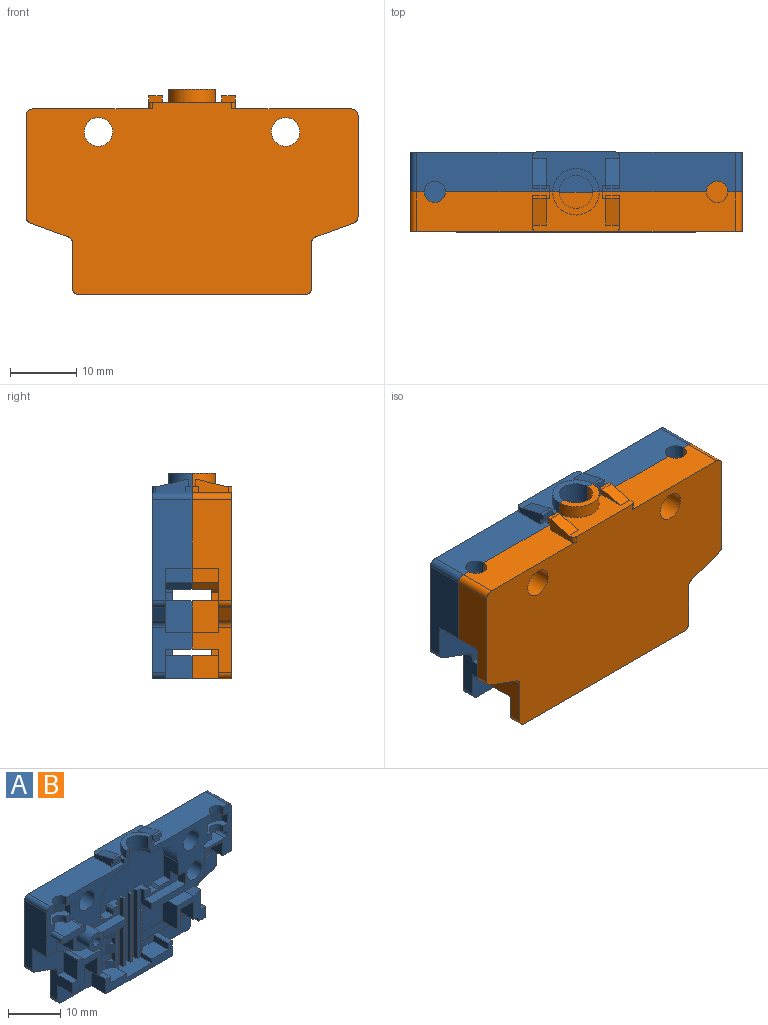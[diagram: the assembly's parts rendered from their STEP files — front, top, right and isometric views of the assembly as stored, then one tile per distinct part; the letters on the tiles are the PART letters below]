
ASSEMBLY  parts=2 mates=1
PART A: 210 faces, bbox 50x9.5x31 mm
  f0: plane 5.51x4.95mm, normal (0,-1,0), area 21mm2, adj f49,f136,f137,f138,f139
  f1: plane 2x1.1mm, normal (1,0,0), area 2.2mm2, adj f76,f185,f203,f205
  f2: plane 6.8x5.5mm, normal (0,-1,0), area 31.4mm2, adj f4,f76,f77,f78,f200,f201,f206,f207
  f3: plane 10.56x0.5mm, normal (0,-1,0), area 5mm2, adj f50,f138,f202,f203
  f4: plane 1.5x1mm, normal (1,0,0), area 1.5mm2, adj f2,f185,f201,f207
  f5: plane 2x0.05mm, normal (0,-1,0), area 0.1mm2, adj f8,f69,f78,f188
  f6: plane 2.85x1.5mm, normal (0,-1,0), area 4.3mm2, adj f7,f69,f70,f199
  f7: plane 4.35x4mm, normal (0,0,1), area 16.6mm2, adj f6,f70,f72,f172,f199
  f8: plane 2x1mm, normal (1,0,0), area 2mm2, adj f5,f69,f78,f185
  f9: plane 5.51x4.95mm, normal (0,-1,0), area 21mm2, adj f131,f132,f133,f134,f135
  f10: plane 6.8x5.5mm, normal (0,-1,0), area 31.4mm2, adj f13,f88,f92,f93,f191,f192,f197,f198
  f11: plane 2x1.1mm, normal (-1,0,0), area 2.2mm2, adj f93,f183,f194,f196
  f12: plane 10.56x0.5mm, normal (0,-1,0), area 5mm2, adj f15,f131,f193,f194
  f13: plane 1.5x1mm, normal (-1,0,0), area 1.5mm2, adj f10,f183,f192,f198
  f14: plane 9.67x8.45mm, normal (0,-1,0), area 39.2mm2, adj f51,f56,f57,f64,f65,f85,f94,f95
  f15: plane 12.06x4mm, normal (0,0,-1), area 47.5mm2, adj f12,f28,f131,f170,f193
  f16: plane 2x0.05mm, normal (0,-1,0), area 0.1mm2, adj f17,f66,f88,f186
  f17: plane 2x1mm, normal (-1,0,0), area 2mm2, adj f16,f66,f88,f183
  f18: plane 4.25x3.55mm, normal (0,-1,0), area 15.1mm2, adj f78,f79,f80,f81
  f19: plane 9x4.5mm, normal (0,-1,0), area 33.1mm2, adj f52,f53,f59,f68,f69,f82,f83
  f20: plane 4.25x3.55mm, normal (0,-1,0), area 15.1mm2, adj f88,f89,f90,f91
  f21: plane 2.85x1.5mm, normal (0,-1,0), area 4.3mm2, adj f26,f66,f71,f190
  f22: plane 9.67x8.45mm, normal (0,-1,0), area 39.2mm2, adj f48,f53,f54,f60,f61,f73,f74,f75
  f23: plane 7x4mm, normal (0,0,1), area 25mm2, adj f24,f72,f172,f173,f175,f176,f177,f178
  f24: plane 26x21.1mm, normal (0,-1,0), area 273mm2, adj f23,f29,f36,f37,f141,f142,f143,f158
  f25: plane 9x4.5mm, normal (0,-1,0), area 33.1mm2, adj f52,f57,f66,f67,f86,f87,f140
  f26: plane 4.35x4mm, normal (0,0,1), area 16.6mm2, adj f21,f71,f72,f173,f190
  f27: plane 9x2mm, normal (0,0,1), area 18mm2, adj f28,f30,f35,f170
  f28: plane 22.5x17.5mm, normal (0,-1,0), area 131.9mm2, adj f15,f27,f34,f35,f36,f37,f38,f40
  f29: plane 2x2mm, normal (0,0,1), area 3mm2, adj f24,f30,f159,f170,f182,f183
  f30: plane 9x3mm, normal (0,-1,0), area 13.2mm2, adj f27,f29,f34,f35,f36,f159,f160,f161
  f31: plane 3x2mm, normal (-1,0,0), area 6mm2, adj f32,f33,f39,f164
  f32: plane 2x1.95mm, normal (0,0,-1), area 3.9mm2, adj f31,f39,f142,f164
  f33: plane 9x2mm, normal (0,0,1), area 18mm2, adj f31,f39,f164,f171
  f34: plane 2x1.95mm, normal (0,0,-1), area 3.9mm2, adj f28,f30,f35,f36
  f35: plane 3x2mm, normal (1,0,0), area 6mm2, adj f27,f28,f30,f34
  f36: plane 5x4mm, normal (1,0,0), area 16mm2, adj f24,f28,f30,f34,f141,f163
  f37: plane 9.1x4mm, normal (0,0,-1), area 22.3mm2, adj f24,f28,f39,f141,f143,f157
  f38: cylinder r=2.5mm len=5mm, axis (0,0,1), area 23.6mm2, adj f28,f39,f40,f156
  f39: plane 22.5x17.5mm, normal (0,-1,0), area 131.3mm2, adj f31,f32,f33,f37,f38,f40,f41,f42
  f40: plane 7x3.5mm, normal (0,0,1), area 9.4mm2, adj f28,f38,f39,f155
  f41: plane 13x6mm, normal (0,0,1), area 37.7mm2, adj f28,f39,f43,f45,f58,f144,f148,f149
  f42: plane 20x6mm, normal (0,0,1), area 103.5mm2, adj f39,f58,f62,f109,f148,f149,f154,f209
  f43: plane 2.5x1mm, normal (0,-1,0), area 2.5mm2, adj f41,f44,f55,f150,f153
  f44: plane 2x0.5mm, normal (0,0,-1), area 1mm2, adj f43,f47,f150,f152
  f45: plane 4x2mm, normal (0,0.24,0.97), area 8.2mm2, adj f41,f46,f150,f152
  f46: plane 2x0.5mm, normal (0,0,1), area 1mm2, adj f45,f47,f150,f152
  f47: plane 2x1mm, normal (0,-1,0), area 2mm2, adj f44,f46,f150,f152
  f48: plane 15.25x6mm, normal (1,0,0), area 71.8mm2, adj f22,f39,f58,f61,f62,f139
  f49: plane 4x3.33mm, normal (-1,0,0), area 13.3mm2, adj f0,f39,f136,f139
  f50: plane 12.06x4mm, normal (0,0,-1), area 47.5mm2, adj f3,f39,f138,f171,f202
  f51: plane 15.25x6mm, normal (-1,0,0), area 71.8mm2, adj f14,f28,f58,f63,f64,f135
  f52: plane 34x6mm, normal (0,0,-1), area 140mm2, adj f19,f25,f58,f59,f67,f68,f72,f140
  f53: plane 6.8x6mm, normal (1,0,0), area 23.6mm2, adj f19,f22,f58,f59,f60,f73,f83,f84
  f54: plane 5.68x2.07mm, normal (0.34,0,-0.94), area 12.1mm2, adj f22,f58,f60,f61
  f55: plane 20x6mm, normal (0,0,1), area 103.5mm2, adj f28,f43,f58,f63,f111,f150,f153,f208
  f56: plane 5.68x2.07mm, normal (-0.34,0,-0.94), area 12.1mm2, adj f14,f58,f64,f65
  f57: plane 6.8x6mm, normal (-1,0,0), area 23.6mm2, adj f14,f25,f58,f65,f85,f86,f96,f140
  f58: plane 50x29mm, normal (0,1,0), area 1245.3mm2, adj f41,f42,f48,f51,f52,f53,f54,f55
  f59: cylinder r=1mm len=2mm, axis (0,1,0), area 3.1mm2, adj f19,f52,f53,f58
  f60: cylinder r=1mm len=2mm, axis (0,-1,0), area 2.4mm2, adj f22,f53,f54,f58
  f61: cylinder r=1mm len=2mm, axis (0,-1,0), area 2.4mm2, adj f22,f48,f54,f58
  f62: cylinder r=1mm len=6mm, axis (0,1,0), area 9.4mm2, adj f39,f42,f48,f58
  f63: cylinder r=1mm len=6mm, axis (0,-1,0), area 9.4mm2, adj f28,f51,f55,f58
  f64: cylinder r=1mm len=2mm, axis (0,-1,0), area 2.4mm2, adj f14,f51,f56,f58
  f65: cylinder r=1mm len=2mm, axis (0,1,0), area 2.4mm2, adj f14,f56,f57,f58
  f66: plane 12.7x4.1mm, normal (0,0,1), area 6.6mm2, adj f16,f17,f21,f25,f67,f71,f72,f87
  f67: plane 4x3.5mm, normal (-1,0,0), area 14mm2, adj f25,f52,f66,f72
  f68: plane 4x3.5mm, normal (1,0,0), area 14mm2, adj f19,f52,f69,f72
  f69: plane 12.7x4.1mm, normal (0,0,1), area 6.6mm2, adj f5,f6,f8,f19,f68,f70,f72,f82
  f70: plane 4x1.5mm, normal (-1,0,0), area 6mm2, adj f6,f7,f69,f72
  f71: plane 4x1.5mm, normal (1,0,0), area 6mm2, adj f21,f26,f66,f72
  f72: plane 18x3.5mm, normal (0,-1,0), area 32.4mm2, adj f7,f23,f26,f52,f66,f67,f68,f69
  f73: plane 4x1.45mm, normal (0,0,1), area 5.8mm2, adj f22,f53,f74,f84
  f74: plane 4.75x4mm, normal (1,0,0), area 19mm2, adj f22,f73,f75,f84
  f75: plane 8.9x4.1mm, normal (-0.4,0,0.91), area 8.4mm2, adj f22,f74,f76,f84,f204,f205
  f76: plane 11.35x4.1mm, normal (0,0,1), area 20.1mm2, adj f1,f2,f75,f77,f84,f205,f206
  f77: plane 5.5x4mm, normal (-1,0,0), area 22mm2, adj f2,f76,f78,f84
  f78: plane 12.7x4.1mm, normal (0,0,-1), area 11.4mm2, adj f2,f5,f8,f18,f77,f79,f81,f82
  f79: plane 4.25x4mm, normal (1,0,0), area 17mm2, adj f18,f78,f80,f84
  f80: plane 4x3.55mm, normal (0,0,-1), area 14.2mm2, adj f18,f79,f81,f84
  f81: plane 4.25x4mm, normal (-1,0,0), area 17mm2, adj f18,f78,f80,f84
  f82: plane 4.1x2mm, normal (-1,0,0), area 4.2mm2, adj f19,f69,f78,f83,f84,f189
  f83: plane 4x1.8mm, normal (0,0,-1), area 7.2mm2, adj f19,f53,f82,f84
  f84: plane 7.7x7.25mm, normal (0,-1,0), area 23.9mm2, adj f53,f73,f74,f75,f76,f77,f78,f79
  f85: plane 4x1.45mm, normal (0,0,1), area 5.8mm2, adj f14,f57,f95,f96
  f86: plane 4x1.8mm, normal (0,0,-1), area 7.2mm2, adj f25,f57,f87,f96
  f87: plane 4.1x2mm, normal (1,0,0), area 4.2mm2, adj f25,f66,f86,f88,f96,f187
  f88: plane 12.7x4.1mm, normal (0,0,-1), area 11.4mm2, adj f10,f16,f17,f20,f87,f89,f91,f92
  f89: plane 4.25x4mm, normal (1,0,0), area 17mm2, adj f20,f88,f90,f96
  f90: plane 4x3.55mm, normal (0,0,-1), area 14.2mm2, adj f20,f89,f91,f96
  f91: plane 4.25x4mm, normal (-1,0,0), area 17mm2, adj f20,f88,f90,f96
  f92: plane 5.5x4mm, normal (1,0,0), area 22mm2, adj f10,f88,f93,f96
  f93: plane 11.35x4.1mm, normal (0,0,1), area 20.1mm2, adj f10,f11,f92,f94,f96,f196,f197
  f94: plane 8.9x4.1mm, normal (0.4,0,0.91), area 8.4mm2, adj f14,f93,f95,f96,f195,f196
  f95: plane 4.75x4mm, normal (-1,0,0), area 19mm2, adj f14,f85,f94,f96
  f96: plane 7.7x7.25mm, normal (0,-1,0), area 23.9mm2, adj f57,f85,f86,f87,f88,f89,f90,f91
  f97: plane 2.5x1.59mm, normal (-1,0,0), area 4mm2, adj f28,f98,f101,f102
  f98: plane 2.75x2.5mm, normal (-0.5,-0.87,0), area 7.9mm2, adj f97,f99,f101,f102
  f99: plane 2.75x2.5mm, normal (0.5,-0.87,0), area 7.9mm2, adj f98,f100,f101,f102
  f100: plane 2.5x1.59mm, normal (1,0,0), area 4mm2, adj f28,f99,f101,f102
  f101: plane 5.5x3.18mm, normal (0,0,1), area 9.1mm2, adj f28,f97,f98,f99,f100,f112
  f102: plane 5.5x3.18mm, normal (0,0,-1), area 9.1mm2, adj f28,f97,f98,f99,f100,f111
  f103: plane 2.75x2.5mm, normal (-0.5,-0.87,0), area 7.9mm2, adj f104,f106,f107,f108
  f104: plane 2.75x2.5mm, normal (0.5,-0.87,0), area 7.9mm2, adj f103,f105,f107,f108
  f105: plane 2.5x1.59mm, normal (1,0,0), area 4mm2, adj f39,f104,f107,f108
  f106: plane 2.5x1.59mm, normal (-1,0,0), area 4mm2, adj f39,f103,f107,f108
  f107: plane 5.5x3.18mm, normal (0,0,1), area 9.1mm2, adj f39,f103,f104,f105,f106,f110
  f108: plane 5.5x3.18mm, normal (0,0,-1), area 9.1mm2, adj f39,f103,f104,f105,f106,f109
  f109: cylinder r=1.6mm len=3.2mm, axis (0,0,1), area 10.1mm2, adj f39,f42,f108
  f110: cylinder r=1.6mm len=3.2mm, axis (0,0,1), area 7.5mm2, adj f39,f107,f118
  f111: cylinder r=1.6mm len=3.2mm, axis (0,0,1), area 10.1mm2, adj f28,f55,f102
  f112: cylinder r=1.6mm len=3.2mm, axis (0,0,1), area 7.5mm2, adj f28,f101,f113
  f113: plane 5x4.6mm, normal (0,0,1), area 19mm2, adj f28,f112,f114,f115,f117
  f114: cylinder r=0.75mm len=3mm, axis (0,1,0), area 7.1mm2, adj f28,f113,f116,f117
  f115: cylinder r=0.75mm len=3mm, axis (0,1,0), area 7.1mm2, adj f28,f113,f116,f117
  f116: plane 5x3mm, normal (0,0,-1), area 15mm2, adj f28,f114,f115,f117
  f117: plane 6.5x1.5mm, normal (0,-1,0), area 9.3mm2, adj f113,f114,f115,f116
  f118: plane 5x3mm, normal (0,0,-1), area 11mm2, adj f39,f110,f119,f121,f122
  f119: cylinder r=0.75mm len=3mm, axis (0,-1,0), area 7.1mm2, adj f39,f118,f120,f122
  f120: plane 5x3mm, normal (0,0,1), area 15mm2, adj f39,f119,f121,f122
  f121: cylinder r=0.75mm len=3mm, axis (0,-1,0), area 7.1mm2, adj f39,f118,f120,f122
  f122: plane 6.5x1.5mm, normal (0,-1,0), area 9.3mm2, adj f118,f119,f120,f121
  f123: cylinder r=2.15mm len=6mm, axis (0,-1,0), area 81.1mm2, adj f39,f58
  f124: cylinder r=2.15mm len=6mm, axis (0,-1,0), area 81.1mm2, adj f28,f58
  f125: cylinder r=2mm len=4mm, axis (0,1,0), area 44mm2, adj f28,f126
  f126: plane 4x4mm, normal (0,-1,0), area 9.4mm2, adj f125,f129
  f127: cylinder r=2.05mm len=5mm, axis (0,-1,0), area 64.4mm2, adj f39,f128
  f128: plane 4.1x4.1mm, normal (0,-1,0), area 13.2mm2, adj f127
  f129: cylinder r=1mm len=5.5mm, axis (0,-1,0), area 34.6mm2, adj f126,f130
  f130: plane 2x2mm, normal (0,-1,0), area 3.1mm2, adj f129
  f131: plane 8.32x4.1mm, normal (-0.4,0,-0.91), area 10.7mm2, adj f9,f12,f15,f28,f132,f194,f195,f196
  f132: plane 5.51x4mm, normal (-1,0,0), area 22.1mm2, adj f9,f28,f131,f133
  f133: plane 4.7x4mm, normal (0,0,-1), area 18.8mm2, adj f9,f28,f132,f134
  f134: plane 4x3.33mm, normal (1,0,0), area 13.3mm2, adj f9,f28,f133,f135
  f135: plane 4x2.5mm, normal (0,0,-1), area 10mm2, adj f9,f14,f28,f51,f134
  f136: plane 4.7x4mm, normal (0,0,-1), area 18.8mm2, adj f0,f39,f49,f137
  f137: plane 5.51x4mm, normal (1,0,0), area 22.1mm2, adj f0,f39,f136,f138
  f138: plane 8.32x4.1mm, normal (0.4,0,-0.91), area 10.7mm2, adj f0,f3,f39,f50,f137,f203,f204,f205
  f139: plane 4x2.5mm, normal (0,0,-1), area 10mm2, adj f0,f22,f39,f48,f49
  f140: cylinder r=1mm len=2mm, axis (0,1,0), area 3.1mm2, adj f25,f52,f57,f58
  f141: cylinder r=6mm len=6mm, axis (0,-1,0), area 37.7mm2, adj f24,f28,f36,f37
  f142: plane 5x4mm, normal (-1,0,0), area 16mm2, adj f24,f32,f39,f143,f164,f165
  f143: cylinder r=6mm len=6mm, axis (0,-1,0), area 37.7mm2, adj f24,f37,f39,f142
  f144: plane 4x2mm, normal (0,0.24,0.97), area 8.2mm2, adj f41,f145,f149,f151
  f145: plane 2x0.5mm, normal (0,0,1), area 1mm2, adj f144,f146,f149,f151
  f146: plane 2x1mm, normal (0,-1,0), area 2mm2, adj f145,f147,f149,f151
  f147: plane 2x0.5mm, normal (0,0,-1), area 1mm2, adj f146,f148,f149,f151
  f148: plane 2.5x1mm, normal (0,-1,0), area 2.5mm2, adj f41,f42,f147,f149,f154
  f149: plane 5x2mm, normal (1,0,0), area 7mm2, adj f41,f42,f144,f145,f146,f147,f148,f209
  f150: plane 5x2mm, normal (-1,0,0), area 7mm2, adj f41,f43,f44,f45,f46,f47,f55,f208
  f151: plane 4.5x1mm, normal (-1,0,0), area 2.5mm2, adj f41,f144,f145,f146,f147
  f152: plane 4.5x1mm, normal (1,0,0), area 2.5mm2, adj f41,f44,f45,f46,f47
  f153: plane 1x1mm, normal (-1,0,0), area 1mm2, adj f28,f41,f43,f55
  f154: plane 1x1mm, normal (1,0,0), area 1mm2, adj f39,f41,f42,f148
  f155: cylinder r=3.5mm len=7mm, axis (0,0,-1), area 22mm2, adj f28,f39,f40,f41
  f156: plane 6x3mm, normal (0,0,-1), area 4.3mm2, adj f28,f38,f39,f157
  f157: cylinder r=3mm len=6mm, axis (0,0,1), area 9.4mm2, adj f28,f37,f39,f156
  f158: plane 2x2mm, normal (0,0,1), area 3mm2, adj f24,f164,f169,f171,f184,f185
  f159: cylinder r=0.5mm len=2mm, axis (0,1,0), area 1.6mm2, adj f24,f29,f30,f160
  f160: plane 2x1mm, normal (-1,0,0), area 2mm2, adj f24,f30,f159,f161
  f161: plane 2x2mm, normal (0,0,1), area 4mm2, adj f24,f30,f160,f162
  f162: plane 2x0.55mm, normal (0.67,0,0.74), area 1.5mm2, adj f24,f30,f161,f163
  f163: plane 3x2mm, normal (0,0,1), area 6mm2, adj f24,f30,f36,f162
  f164: plane 9x3mm, normal (0,-1,0), area 13.2mm2, adj f31,f32,f33,f142,f158,f165,f166,f167
  f165: plane 3x2mm, normal (0,0,1), area 6mm2, adj f24,f142,f164,f166
  f166: plane 2x0.55mm, normal (-0.67,0,0.74), area 1.5mm2, adj f24,f164,f165,f167
  f167: plane 2x2mm, normal (0,0,1), area 4mm2, adj f24,f164,f166,f168
  f168: plane 2x1mm, normal (1,0,0), area 2mm2, adj f24,f164,f167,f169
  f169: cylinder r=0.5mm len=2mm, axis (0,1,0), area 1.6mm2, adj f24,f158,f164,f168
  f170: plane 3.5x3mm, normal (1,0,0), area 6.5mm2, adj f15,f27,f28,f29,f30,f183
  f171: plane 3.5x3mm, normal (-1,0,0), area 6.5mm2, adj f33,f39,f50,f158,f164,f185
  f172: plane 3x1mm, normal (-1,0,0), area 3mm2, adj f7,f23,f72,f185
  f173: plane 3x1mm, normal (1,0,0), area 3mm2, adj f23,f26,f72,f183
  f174: plane 1x0.5mm, normal (0,0,1), area 0.5mm2, adj f24,f175,f176,f177
  f175: plane 16x1mm, normal (-1,0,0), area 16mm2, adj f23,f24,f174,f177
  f176: plane 16x1mm, normal (1,0,0), area 16mm2, adj f23,f24,f174,f177
  f177: plane 16x0.5mm, normal (0,-1,0), area 8mm2, adj f23,f174,f175,f176
  f178: plane 16x1mm, normal (1,0,0), area 16mm2, adj f23,f24,f179,f181
  f179: plane 1x0.5mm, normal (0,0,1), area 0.5mm2, adj f24,f178,f180,f181
  f180: plane 16x1mm, normal (-1,0,0), area 16mm2, adj f23,f24,f179,f181
  f181: plane 16x0.5mm, normal (0,-1,0), area 8mm2, adj f23,f178,f179,f180
  f182: plane 16x1mm, normal (1,0,0), area 16mm2, adj f23,f24,f29,f183
  f183: plane 16x1mm, normal (0,-1,0), area 16mm2, adj f11,f13,f17,f23,f29,f170,f173,f182
  f184: plane 16x1mm, normal (-1,0,0), area 16mm2, adj f23,f24,f158,f185
  f185: plane 16x1mm, normal (0,-1,0), area 16mm2, adj f1,f4,f8,f23,f158,f171,f172,f184
  f186: plane 2x0.1mm, normal (-1,0,0), area 0.2mm2, adj f16,f66,f88,f187
  f187: plane 12.65x2mm, normal (0,-1,0), area 25.3mm2, adj f66,f87,f88,f186
  f188: plane 2x0.1mm, normal (1,0,0), area 0.2mm2, adj f5,f69,f78,f189
  f189: plane 12.65x2mm, normal (0,-1,0), area 25.3mm2, adj f69,f78,f82,f188
  f190: plane 1.5x1.5mm, normal (-0.55,-0.83,0), area 2.7mm2, adj f21,f26,f66,f183
  f191: plane 2x1.5mm, normal (-0.55,-0.83,0), area 3.6mm2, adj f10,f88,f183,f192
  f192: plane 1.5x1mm, normal (0,0,1), area 0.8mm2, adj f10,f13,f191
  f193: plane 1.5x1mm, normal (-0.55,-0.83,0), area 0.9mm2, adj f12,f15,f183,f194
  f194: plane 10.93x1.1mm, normal (0,0,-1), area 1.8mm2, adj f11,f12,f131,f193,f196
  f195: plane 1.74x1mm, normal (0.87,0,-0.5), area 0.2mm2, adj f14,f94,f131,f196
  f196: plane 20.25x5.67mm, normal (0,-1,0), area 41.1mm2, adj f11,f93,f94,f131,f194,f195
  f197: plane 2x1.5mm, normal (-0.55,-0.83,0), area 3.6mm2, adj f10,f93,f183,f198
  f198: plane 1.5x1mm, normal (0,0,-1), area 0.8mm2, adj f10,f13,f197
  f199: plane 1.5x1.5mm, normal (0.55,-0.83,0), area 2.7mm2, adj f6,f7,f69,f185
  f200: plane 2x1.5mm, normal (0.55,-0.83,0), area 3.6mm2, adj f2,f78,f185,f201
  f201: plane 1.5x1mm, normal (0,0,1), area 0.8mm2, adj f2,f4,f200
  f202: plane 1.5x1mm, normal (0.55,-0.83,0), area 0.9mm2, adj f3,f50,f185,f203
  f203: plane 10.93x1.1mm, normal (0,0,-1), area 1.8mm2, adj f1,f3,f138,f202,f205
  f204: plane 1.74x1mm, normal (-0.87,0,-0.5), area 0.2mm2, adj f22,f75,f138,f205
  f205: plane 20.25x5.67mm, normal (0,-1,0), area 41.1mm2, adj f1,f75,f76,f138,f203,f204
  f206: plane 2x1.5mm, normal (0.55,-0.83,0), area 3.6mm2, adj f2,f76,f185,f207
  f207: plane 1.5x1mm, normal (0,0,-1), area 0.8mm2, adj f2,f4,f206
  f208: cylinder r=0.5mm len=1mm, axis (0,0,1), area 0.8mm2, adj f41,f55,f58,f150
  f209: cylinder r=0.5mm len=1mm, axis (0,0,-1), area 0.8mm2, adj f41,f42,f58,f149
PART B: same geometry as A
PLACE A t=(-6.17,1.48,-1.06)mm fixed
PLACE B rot(axis=(0,0,1),180deg) t=(-6.17,-10.52,-1.06)mm
MATE fastened B.f124 <-> A.f123  axis (0,1,0) through (7.93,-4.52,9.49)mm
